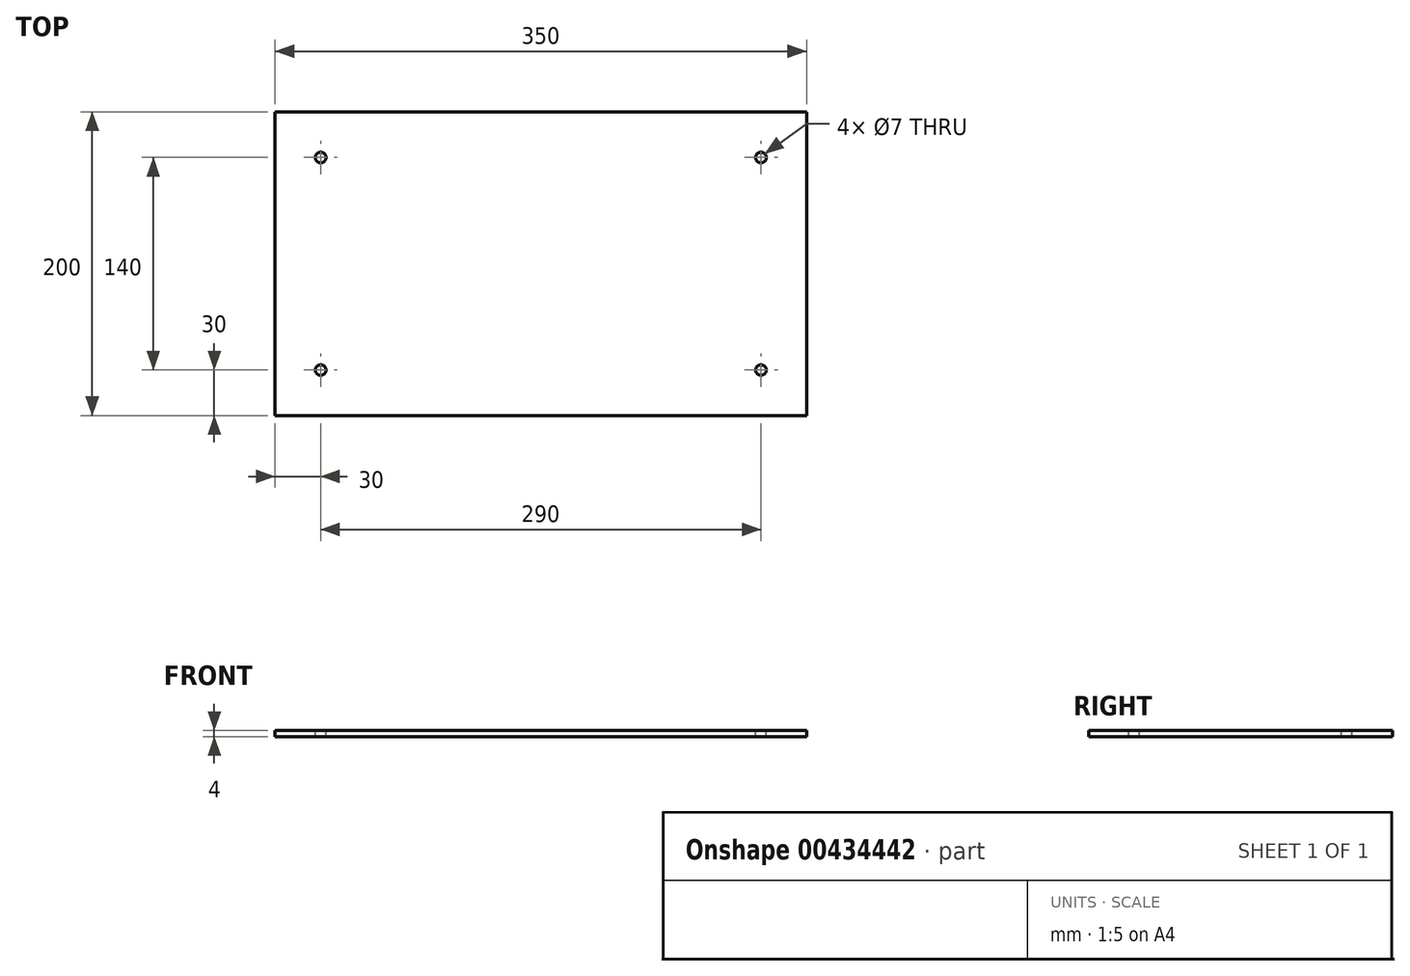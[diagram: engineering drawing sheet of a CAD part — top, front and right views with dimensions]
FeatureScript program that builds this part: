
annotation { "Feature Type Name" : "Feature", "Feature Type Description" : "" }
export const myFeature = defineFeature(function(context is Context, id is Id, definition is map)
    precondition{}
    {
        {
            var Q0;
            Q0=qCreatedBy(makeId("Right.planeOp"),FACE);
            var sketch = newSketch(context, id + "F0", { "sketchPlane" : qUnion([Q0])});
            skLineSegment(sketch, "E0.bottom", {"start": v(-200, 4) * mm, "end": v(0, 4) * mm});
            skLineSegment(sketch, "E1.top", {"start": v(-200, 0) * mm, "end": v(0, 0) * mm});
            skLineSegment(sketch, "E2.trimOffspring", {"start": v(-200, 0) * mm, "end": v(-200, 4) * mm});
            skLineSegment(sketch, "E3", {"start": v(0, 0) * mm, "end": v(0, 4) * mm});
            skSolve(sketch);
        }
        {
            var Q0;
            Q0 = qSketchRegion(id + "F0", true);
            extrude(context, id + "F1", {"entities" : qUnion([Q0]), "endBound" : BoundingType.SYMMETRIC, "depth" : 350 * mm, "offsetDistance" : 25 * mm});
        }
        {
            var Q0;
            Q0=makeQuery(id+"F1.opExtrude","SWEPT_FACE",FACE,{"disambiguationData":[OSD([sQuery(id+"F0.wireOp",EDGE,"E0.bottom")])]});
            var sketch = newSketch(context, id + "F2", { "sketchPlane" : qUnion([Q0])});
            skCircle(sketch, "E4", {"center": v(-145, -170) * mm, "radius": 3.5 * mm});
            skCircle(sketch, "E5", {"center": v(-145, -30) * mm, "radius": 3.5 * mm});
            skCircle(sketch, "E6", {"center": v(145, -30) * mm, "radius": 3.5 * mm});
            skCircle(sketch, "E7", {"center": v(145, -170) * mm, "radius": 3.5 * mm});
            skSolve(sketch);
        }
        {
            var Q0;
            Q0 = qSketchRegion(id + "F2", true);
            extrude(context, id + "F3", {"entities" : qUnion([Q0]), "operationType" : NewBodyOperationType.REMOVE, "endBound" : BoundingType.UP_TO_NEXT, "oppositeDirection" : true, "depth" : 25 * mm, "offsetDistance" : 25 * mm});
        }
    });
